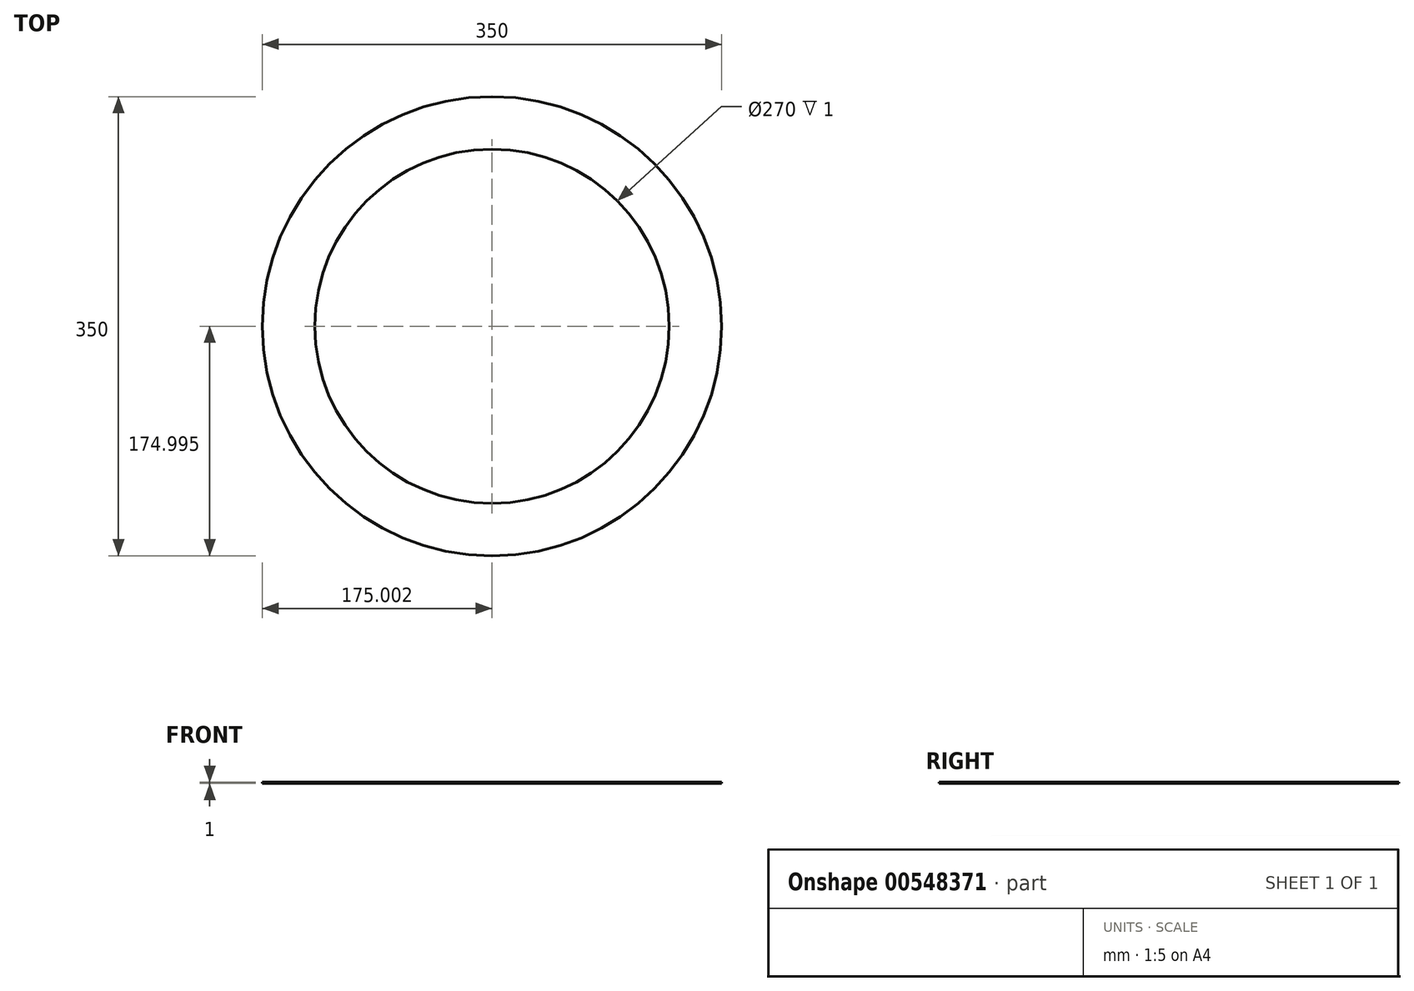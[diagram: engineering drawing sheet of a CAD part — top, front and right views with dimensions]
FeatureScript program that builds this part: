
annotation { "Feature Type Name" : "Feature", "Feature Type Description" : "" }
export const myFeature = defineFeature(function(context is Context, id is Id, definition is map)
    precondition{}
    {
        {
            var Q0;
            Q0=qCreatedBy(makeId("Top.planeOp"),FACE);
            var sketch = newSketch(context, id + "F0", { "sketchPlane" : qUnion([Q0])});
            skCircle(sketch, "E0", {"center": v(-67.96, -9.2) * mm, "radius": 135 * mm});
            skCircle(sketch, "E1.0", {"center": v(-67.96, -9.2) * mm, "radius": 175 * mm});
            skSolve(sketch);
        }
        {
            var Q0;
            Q0=makeQuery(id+"F0.imprint","IMPRINT",FACE,{"disambiguationData":[TD([[makeQuery(id+"F0.imprint","IMPRINT",EDGE,{"derivedFrom":sQuery(id+"F0.wireOp",EDGE,"E0")}),-1.0]])]});
            extrude(context, id + "F1", {"entities" : qUnion([Q0]), "depth" : 1 * mm, "offsetDistance" : 25 * mm});
        }
    });
